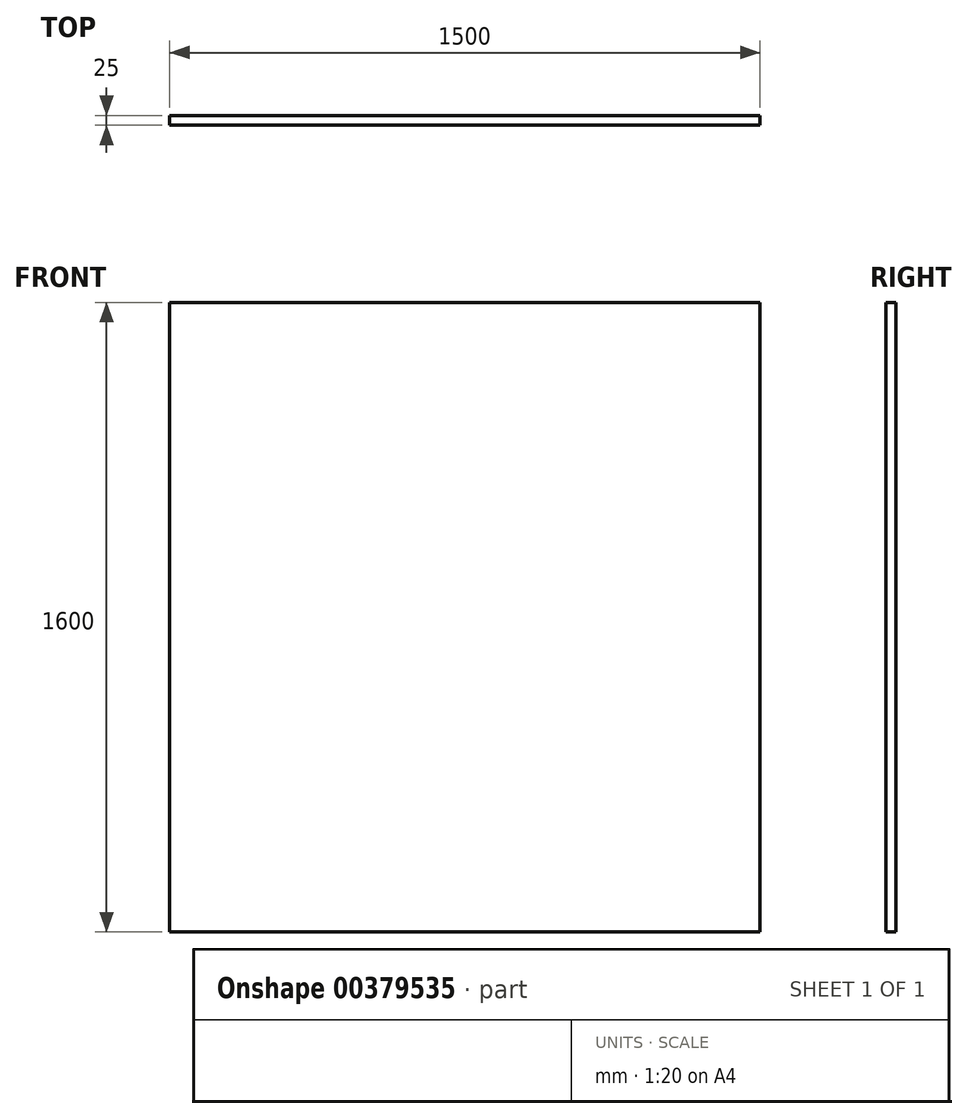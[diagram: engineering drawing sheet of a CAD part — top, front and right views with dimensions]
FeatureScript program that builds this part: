
annotation { "Feature Type Name" : "Feature", "Feature Type Description" : "" }
export const myFeature = defineFeature(function(context is Context, id is Id, definition is map)
    precondition{}
    {
        {
            var Q0;
            Q0=qCreatedBy(makeId("Front.planeOp"),FACE);
            var sketch = newSketch(context, id + "F0", { "sketchPlane" : qUnion([Q0])});
            skLineSegment(sketch, "E0.bottom", {"start": v(-785.21, 927.23) * mm, "end": v(714.79, 927.23) * mm});
            skLineSegment(sketch, "E0.top", {"start": v(-785.21, -672.77) * mm, "end": v(714.79, -672.77) * mm});
            skLineSegment(sketch, "E0.left", {"start": v(-785.21, 927.23) * mm, "end": v(-785.21, -672.77) * mm});
            skLineSegment(sketch, "E0.right", {"start": v(714.79, 927.23) * mm, "end": v(714.79, -672.77) * mm});
            skSolve(sketch);
        }
        {
            var Q0;
            Q0=makeQuery(id+"F0.imprint","IMPRINT",FACE,{"disambiguationData":[TD([[makeQuery(id+"F0.imprint","IMPRINT",EDGE,{"derivedFrom":sQuery(id+"F0.wireOp",EDGE,"E0.bottom")}),-1.0]])]});
            extrude(context, id + "F1", {"entities" : qUnion([Q0]), "depth" : 25 * mm});
        }
    });
